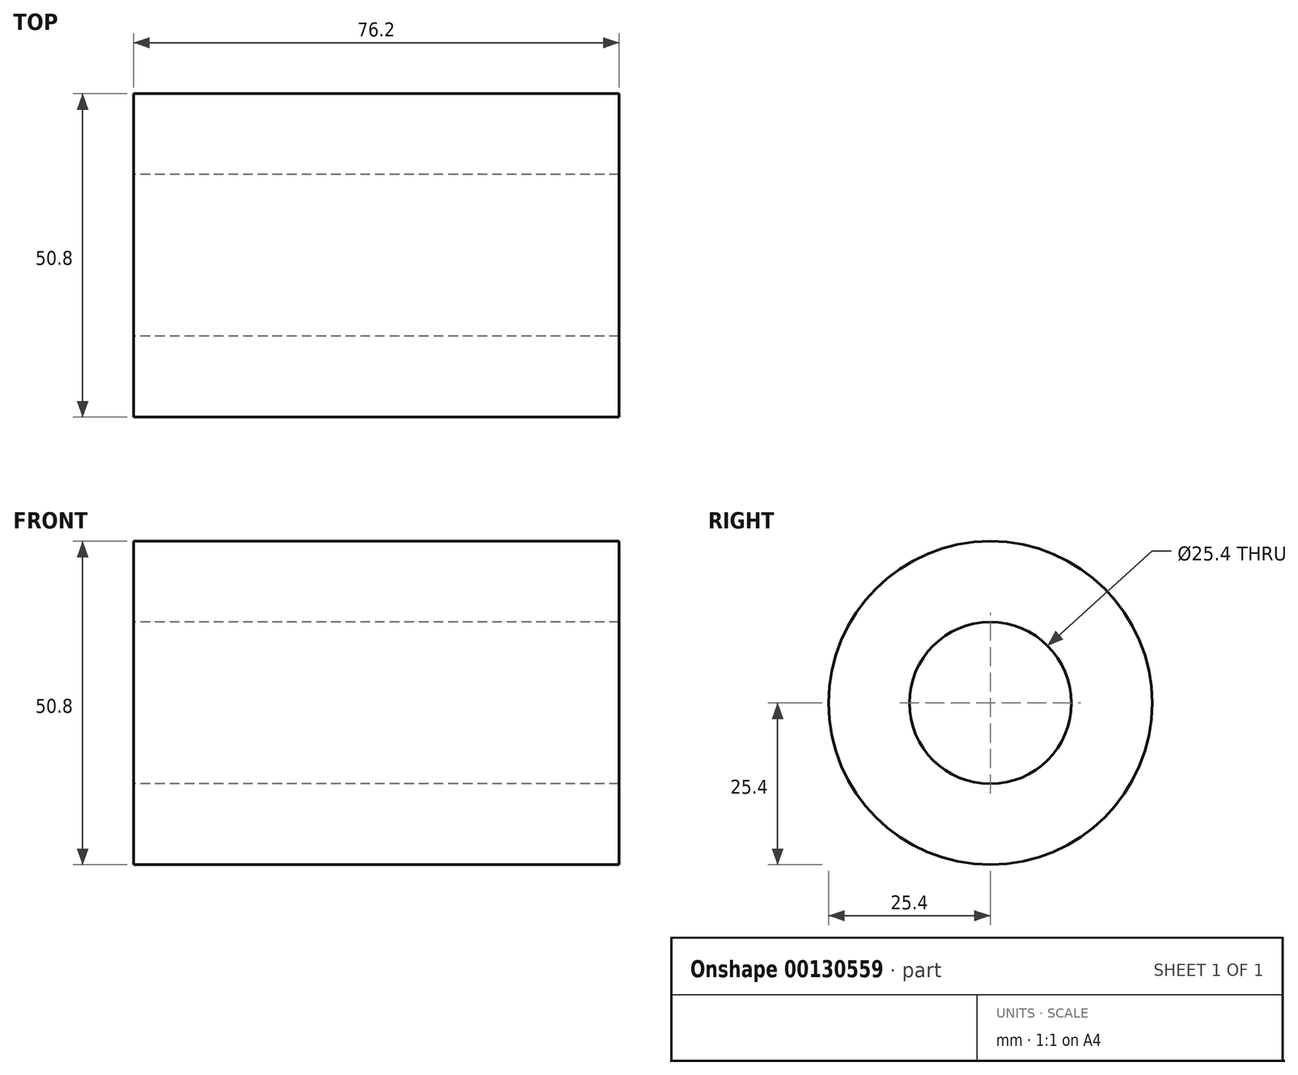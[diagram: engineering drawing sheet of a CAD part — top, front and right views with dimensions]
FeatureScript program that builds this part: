
annotation { "Feature Type Name" : "Feature", "Feature Type Description" : "" }
export const myFeature = defineFeature(function(context is Context, id is Id, definition is map)
    precondition{}
    {
        {
            var Q0;
            Q0=qCreatedBy(makeId("Right.planeOp"),FACE);
            var sketch = newSketch(context, id + "F0", { "sketchPlane" : qUnion([Q0])});
            skCircle(sketch, "E0", {"center": v(0, 0) * mm, "radius": 12.7 * mm});
            skCircle(sketch, "E1", {"center": v(0, 0) * mm, "radius": 25.4 * mm});
            skLineSegment(sketch, "E2", {"start": v(16.76, 38.1) * mm, "end": v(16.76, 50.8) * mm});
            skLineSegment(sketch, "E3", {"start": v(16.76, 50.8) * mm, "end": v(25.84, 50.8) * mm});
            skLineSegment(sketch, "E4", {"start": v(25.4, 0) * mm, "end": v(25.84, 50.8) * mm});
            skLineSegment(sketch, "E5", {"start": v(16.76, 38.1) * mm, "end": v(-8.64, 38.1) * mm});
            skLineSegment(sketch, "E6", {"start": v(-8.64, 38.1) * mm, "end": v(-8.64, 23.89) * mm});
            skLineSegment(sketch, "E7", {"start": v(16.76, 38.1) * mm, "end": v(25.73, 38.1) * mm});
            skSolve(sketch);
        }
        {
            var Q0;
            Q0=makeQuery(id+"F0.imprint","IMPRINT",FACE,{"disambiguationData":[TD([[makeQuery(id+"F0.imprint","IMPRINT",EDGE,{"derivedFrom":sQuery(id+"F0.wireOp",EDGE,"E0")}),-1.0]])]});
            extrude(context, id + "F1", {"entities" : qUnion([Q0]), "depth" : 76.2 * mm});
        }
    });
